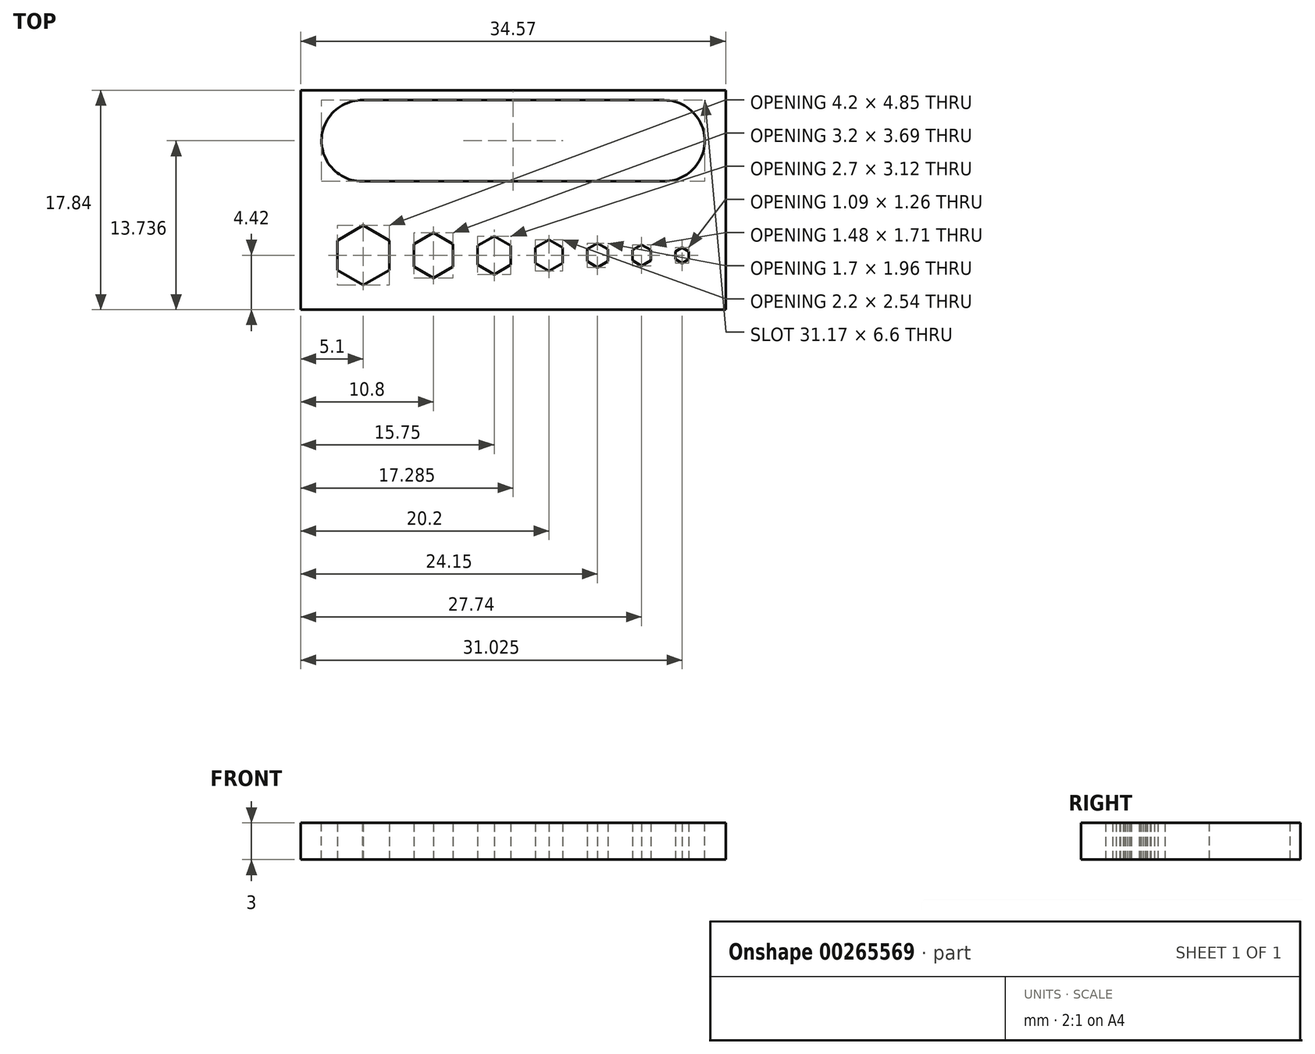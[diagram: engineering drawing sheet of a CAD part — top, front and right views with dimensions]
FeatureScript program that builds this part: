
annotation { "Feature Type Name" : "Feature", "Feature Type Description" : "" }
export const myFeature = defineFeature(function(context is Context, id is Id, definition is map)
    precondition{}
    {
        {
            var Q0;
            Q0=qCreatedBy(makeId("Top.planeOp"),FACE);
            var sketch = newSketch(context, id + "F0", { "sketchPlane" : qUnion([Q0])});
            skCircle(sketch, "E0.cCircle", {"center": v(0, 0) * mm, "radius": 1.1 * mm, "construction": true});
            skLineSegment(sketch, "E0.0", {"start": v(1.1, 0.64) * mm, "end": v(1.1, -0.64) * mm});
            skLineSegment(sketch, "E0.1", {"start": v(1.1, -0.64) * mm, "end": v(0, -1.27) * mm});
            skLineSegment(sketch, "E0.2", {"start": v(0, -1.27) * mm, "end": v(-1.1, -0.64) * mm});
            skLineSegment(sketch, "E0.3", {"start": v(-1.1, -0.64) * mm, "end": v(-1.1, 0.64) * mm});
            skLineSegment(sketch, "E0.4", {"start": v(-1.1, 0.64) * mm, "end": v(0, 1.27) * mm});
            skLineSegment(sketch, "E0.5", {"start": v(0, 1.27) * mm, "end": v(1.1, 0.64) * mm});
            skPoint(sketch, "E0.0.midPoint", {"position": v(1.1, 0) * mm});
            skCircle(sketch, "E1.cCircle", {"center": v(3.95, 0) * mm, "radius": 0.85 * mm, "construction": true});
            skLineSegment(sketch, "E1.0", {"start": v(4.8, 0.5) * mm, "end": v(4.8, -0.5) * mm});
            skLineSegment(sketch, "E1.1", {"start": v(4.8, -0.5) * mm, "end": v(3.95, -0.98) * mm});
            skLineSegment(sketch, "E1.2", {"start": v(3.95, -0.98) * mm, "end": v(3.1, -0.5) * mm});
            skLineSegment(sketch, "E1.3", {"start": v(3.1, -0.5) * mm, "end": v(3.1, 0.5) * mm});
            skLineSegment(sketch, "E1.4", {"start": v(3.1, 0.5) * mm, "end": v(3.95, 0.98) * mm});
            skLineSegment(sketch, "E1.5", {"start": v(3.95, 0.98) * mm, "end": v(4.8, 0.5) * mm});
            skPoint(sketch, "E1.0.midPoint", {"position": v(4.8, 0) * mm});
            skCircle(sketch, "E2.cCircle", {"center": v(7.54, 0) * mm, "radius": 0.74 * mm, "construction": true});
            skLineSegment(sketch, "E2.0", {"start": v(8.28, 0.43) * mm, "end": v(8.28, -0.43) * mm});
            skLineSegment(sketch, "E2.1", {"start": v(8.28, -0.43) * mm, "end": v(7.54, -0.85) * mm});
            skLineSegment(sketch, "E2.2", {"start": v(7.54, -0.85) * mm, "end": v(6.8, -0.43) * mm});
            skLineSegment(sketch, "E2.3", {"start": v(6.8, -0.43) * mm, "end": v(6.8, 0.43) * mm});
            skLineSegment(sketch, "E2.4", {"start": v(6.8, 0.43) * mm, "end": v(7.54, 0.85) * mm});
            skLineSegment(sketch, "E2.5", {"start": v(7.54, 0.85) * mm, "end": v(8.28, 0.43) * mm});
            skPoint(sketch, "E2.0.midPoint", {"position": v(8.28, 0) * mm});
            skCircle(sketch, "E3.cCircle", {"center": v(10.82, 0) * mm, "radius": 0.54 * mm, "construction": true});
            skLineSegment(sketch, "E3.0", {"start": v(11.37, 0.31) * mm, "end": v(11.37, -0.31) * mm});
            skLineSegment(sketch, "E3.1", {"start": v(11.37, -0.31) * mm, "end": v(10.82, -0.63) * mm});
            skLineSegment(sketch, "E3.2", {"start": v(10.82, -0.63) * mm, "end": v(10.28, -0.31) * mm});
            skLineSegment(sketch, "E3.3", {"start": v(10.28, -0.31) * mm, "end": v(10.28, 0.31) * mm});
            skLineSegment(sketch, "E3.4", {"start": v(10.28, 0.31) * mm, "end": v(10.83, 0.63) * mm});
            skLineSegment(sketch, "E3.5", {"start": v(10.83, 0.63) * mm, "end": v(11.37, 0.31) * mm});
            skPoint(sketch, "E3.0.midPoint", {"position": v(11.37, 0) * mm});
            skCircle(sketch, "E4.cCircle", {"center": v(-4.45, 0) * mm, "radius": 1.35 * mm, "construction": true});
            skLineSegment(sketch, "E4.0", {"start": v(-3.1, 0.78) * mm, "end": v(-3.1, -0.78) * mm});
            skLineSegment(sketch, "E4.1", {"start": v(-3.1, -0.78) * mm, "end": v(-4.45, -1.56) * mm});
            skLineSegment(sketch, "E4.2", {"start": v(-4.45, -1.56) * mm, "end": v(-5.8, -0.78) * mm});
            skLineSegment(sketch, "E4.3", {"start": v(-5.8, -0.78) * mm, "end": v(-5.8, 0.78) * mm});
            skLineSegment(sketch, "E4.4", {"start": v(-5.8, 0.78) * mm, "end": v(-4.45, 1.56) * mm});
            skLineSegment(sketch, "E4.5", {"start": v(-4.45, 1.56) * mm, "end": v(-3.1, 0.78) * mm});
            skPoint(sketch, "E4.0.midPoint", {"position": v(-3.1, 0) * mm});
            skCircle(sketch, "E5.cCircle", {"center": v(-9.4, 0) * mm, "radius": 1.6 * mm, "construction": true});
            skLineSegment(sketch, "E5.0", {"start": v(-7.8, 0.92) * mm, "end": v(-7.8, -0.92) * mm});
            skLineSegment(sketch, "E5.1", {"start": v(-7.8, -0.92) * mm, "end": v(-9.4, -1.85) * mm});
            skLineSegment(sketch, "E5.2", {"start": v(-9.4, -1.85) * mm, "end": v(-11, -0.92) * mm});
            skLineSegment(sketch, "E5.3", {"start": v(-11, -0.92) * mm, "end": v(-11, 0.92) * mm});
            skLineSegment(sketch, "E5.4", {"start": v(-11, 0.92) * mm, "end": v(-9.4, 1.85) * mm});
            skLineSegment(sketch, "E5.5", {"start": v(-9.4, 1.85) * mm, "end": v(-7.8, 0.92) * mm});
            skPoint(sketch, "E5.0.midPoint", {"position": v(-7.8, 0) * mm});
            skCircle(sketch, "E6.cCircle", {"center": v(-15.1, 0) * mm, "radius": 2.1 * mm, "construction": true});
            skPoint(sketch, "E6.cCircle.centerSnap0", {"position": v(-11, 0) * mm});
            skPoint(sketch, "E6.cCircle.perimeterSnap0", {"position": v(-11, 0) * mm});
            skLineSegment(sketch, "E6.0", {"start": v(-13, 1.21) * mm, "end": v(-13, -1.21) * mm});
            skLineSegment(sketch, "E6.1", {"start": v(-13, -1.21) * mm, "end": v(-15.1, -2.42) * mm});
            skLineSegment(sketch, "E6.2", {"start": v(-15.1, -2.42) * mm, "end": v(-17.2, -1.21) * mm});
            skLineSegment(sketch, "E6.3", {"start": v(-17.2, -1.21) * mm, "end": v(-17.2, 1.21) * mm});
            skLineSegment(sketch, "E6.4", {"start": v(-17.2, 1.21) * mm, "end": v(-15.1, 2.42) * mm});
            skLineSegment(sketch, "E6.5", {"start": v(-15.1, 2.42) * mm, "end": v(-13, 1.21) * mm});
            skPoint(sketch, "E6.0.midPoint", {"position": v(-13, 0) * mm});
            skPoint(sketch, "E6.0.midPoint.positionSnap0", {"position": v(-11, 0) * mm});
            skLineSegment(sketch, "E7.bottom", {"start": v(-20.2, 4.42) * mm, "end": v(14.37, 4.42) * mm});
            skLineSegment(sketch, "E7.top", {"start": v(-20.2, -4.42) * mm, "end": v(14.37, -4.42) * mm});
            skLineSegment(sketch, "E7.left", {"start": v(-20.2, 4.42) * mm, "end": v(-20.2, -4.42) * mm});
            skLineSegment(sketch, "E7.right", {"start": v(14.37, 4.42) * mm, "end": v(14.37, -4.42) * mm});
            skLineSegment(sketch, "E8.top", {"start": v(-20.2, 13.42) * mm, "end": v(14.37, 13.42) * mm});
            skLineSegment(sketch, "E8.left", {"start": v(-20.2, 4.42) * mm, "end": v(-20.2, 13.42) * mm});
            skLineSegment(sketch, "E8.right", {"start": v(14.37, 4.42) * mm, "end": v(14.37, 13.42) * mm});
            skPoint(sketch, "E9.startSnap0", {"position": v(-20.2, 8.92) * mm});
            skPoint(sketch, "E10", {"position": v(-15.2, 8.92) * mm});
            skPoint(sketch, "E11", {"position": v(9.37, 9.53) * mm});
            skSolve(sketch);
        }
        {
            var Q0;
            Q0 = qSketchRegion(id + "F0", true);
            extrude(context, id + "F1", {"entities" : qUnion([Q0]), "depth" : 3 * mm});
        }
        {
            var Q0;
            Q0=makeQuery(id+"F1.opExtrude","CAP_FACE",FACE,{"disambiguationData":[OSD([sQuery(id+"F0.wireOp",EDGE,"E0.0"),sQuery(id+"F0.wireOp",EDGE,"E0.1"),sQuery(id+"F0.wireOp",EDGE,"E0.2"),sQuery(id+"F0.wireOp",EDGE,"E0.3"),sQuery(id+"F0.wireOp",EDGE,"E0.4"),sQuery(id+"F0.wireOp",EDGE,"E0.5"),sQuery(id+"F0.wireOp",EDGE,"E1.0"),sQuery(id+"F0.wireOp",EDGE,"E1.1"),sQuery(id+"F0.wireOp",EDGE,"E1.2"),sQuery(id+"F0.wireOp",EDGE,"E1.3"),sQuery(id+"F0.wireOp",EDGE,"E1.4"),sQuery(id+"F0.wireOp",EDGE,"E1.5"),sQuery(id+"F0.wireOp",EDGE,"E2.0"),sQuery(id+"F0.wireOp",EDGE,"E2.1"),sQuery(id+"F0.wireOp",EDGE,"E2.2"),sQuery(id+"F0.wireOp",EDGE,"E2.3"),sQuery(id+"F0.wireOp",EDGE,"E2.4"),sQuery(id+"F0.wireOp",EDGE,"E2.5"),sQuery(id+"F0.wireOp",EDGE,"E3.0"),sQuery(id+"F0.wireOp",EDGE,"E3.1"),sQuery(id+"F0.wireOp",EDGE,"E3.2"),sQuery(id+"F0.wireOp",EDGE,"E3.3"),sQuery(id+"F0.wireOp",EDGE,"E3.4"),sQuery(id+"F0.wireOp",EDGE,"E3.5"),sQuery(id+"F0.wireOp",EDGE,"E4.0"),sQuery(id+"F0.wireOp",EDGE,"E4.1"),sQuery(id+"F0.wireOp",EDGE,"E4.2"),sQuery(id+"F0.wireOp",EDGE,"E4.3"),sQuery(id+"F0.wireOp",EDGE,"E4.4"),sQuery(id+"F0.wireOp",EDGE,"E4.5"),sQuery(id+"F0.wireOp",EDGE,"E5.0"),sQuery(id+"F0.wireOp",EDGE,"E5.1"),sQuery(id+"F0.wireOp",EDGE,"E5.2"),sQuery(id+"F0.wireOp",EDGE,"E5.3"),sQuery(id+"F0.wireOp",EDGE,"E5.4"),sQuery(id+"F0.wireOp",EDGE,"E5.5"),sQuery(id+"F0.wireOp",EDGE,"E6.0"),sQuery(id+"F0.wireOp",EDGE,"E6.1"),sQuery(id+"F0.wireOp",EDGE,"E6.2"),sQuery(id+"F0.wireOp",EDGE,"E6.3"),sQuery(id+"F0.wireOp",EDGE,"E6.4"),sQuery(id+"F0.wireOp",EDGE,"E6.5"),sQuery(id+"F0.wireOp",EDGE,"E7.top"),sQuery(id+"F0.wireOp",EDGE,"E7.left"),sQuery(id+"F0.wireOp",EDGE,"E7.right"),sQuery(id+"F0.wireOp",EDGE,"E8.top"),sQuery(id+"F0.wireOp",EDGE,"E8.left"),sQuery(id+"F0.wireOp",EDGE,"E8.right")])],"isStart":false});
            var sketch = newSketch(context, id + "F2", { "sketchPlane" : qUnion([Q0])});
            skPoint(sketch, "E12", {"position": v(-15.2, 9.32) * mm});
            skPoint(sketch, "E13", {"position": v(9.37, 9.32) * mm});
            skSolve(sketch);
        }
        {
            var Q0;
            Q0=sQuery(id+"F2.wireOp",VERTEX,"E12");
            var Q1;
            Q1=sQuery(id+"F2.wireOp",VERTEX,"E13");
            var Q2;
            Q2=makeQuery(id+"F1.opExtrude","SWEPT_BODY",BODY,{"disambiguationData":[OSD([sQuery(id+"F0.wireOp",EDGE,"E0.0"),sQuery(id+"F0.wireOp",EDGE,"E0.1"),sQuery(id+"F0.wireOp",EDGE,"E0.2"),sQuery(id+"F0.wireOp",EDGE,"E0.3"),sQuery(id+"F0.wireOp",EDGE,"E0.4"),sQuery(id+"F0.wireOp",EDGE,"E0.5"),sQuery(id+"F0.wireOp",EDGE,"E1.0"),sQuery(id+"F0.wireOp",EDGE,"E1.1"),sQuery(id+"F0.wireOp",EDGE,"E1.2"),sQuery(id+"F0.wireOp",EDGE,"E1.3"),sQuery(id+"F0.wireOp",EDGE,"E1.4"),sQuery(id+"F0.wireOp",EDGE,"E1.5"),sQuery(id+"F0.wireOp",EDGE,"E2.0"),sQuery(id+"F0.wireOp",EDGE,"E2.1"),sQuery(id+"F0.wireOp",EDGE,"E2.2"),sQuery(id+"F0.wireOp",EDGE,"E2.3"),sQuery(id+"F0.wireOp",EDGE,"E2.4"),sQuery(id+"F0.wireOp",EDGE,"E2.5"),sQuery(id+"F0.wireOp",EDGE,"E3.0"),sQuery(id+"F0.wireOp",EDGE,"E3.1"),sQuery(id+"F0.wireOp",EDGE,"E3.2"),sQuery(id+"F0.wireOp",EDGE,"E3.3"),sQuery(id+"F0.wireOp",EDGE,"E3.4"),sQuery(id+"F0.wireOp",EDGE,"E3.5"),sQuery(id+"F0.wireOp",EDGE,"E4.0"),sQuery(id+"F0.wireOp",EDGE,"E4.1"),sQuery(id+"F0.wireOp",EDGE,"E4.2"),sQuery(id+"F0.wireOp",EDGE,"E4.3"),sQuery(id+"F0.wireOp",EDGE,"E4.4"),sQuery(id+"F0.wireOp",EDGE,"E4.5"),sQuery(id+"F0.wireOp",EDGE,"E5.0"),sQuery(id+"F0.wireOp",EDGE,"E5.1"),sQuery(id+"F0.wireOp",EDGE,"E5.2"),sQuery(id+"F0.wireOp",EDGE,"E5.3"),sQuery(id+"F0.wireOp",EDGE,"E5.4"),sQuery(id+"F0.wireOp",EDGE,"E5.5"),sQuery(id+"F0.wireOp",EDGE,"E6.0"),sQuery(id+"F0.wireOp",EDGE,"E6.1"),sQuery(id+"F0.wireOp",EDGE,"E6.2"),sQuery(id+"F0.wireOp",EDGE,"E6.3"),sQuery(id+"F0.wireOp",EDGE,"E6.4"),sQuery(id+"F0.wireOp",EDGE,"E6.5"),sQuery(id+"F0.wireOp",EDGE,"E7.top"),sQuery(id+"F0.wireOp",EDGE,"E7.left"),sQuery(id+"F0.wireOp",EDGE,"E7.right"),sQuery(id+"F0.wireOp",EDGE,"E8.top"),sQuery(id+"F0.wireOp",EDGE,"E8.left"),sQuery(id+"F0.wireOp",EDGE,"E8.right")])]});
            hole(context, id + "F3", {"style" : HoleStyle.SIMPLE, "endStyle" : HoleEndStyle.THROUGH, "standardTappedOrClearance" : lookupTablePath({ "standard" : "ISO", "fit" : "Normal", "size" : "M6", "type" : "Clearance" }), "standardBlindInLast" : lookupTablePath({ "fit" : "Standard", "standard" : "ISO", "size" : "M6", "type" : "Clearance" }), "holeDiameter" : 6.6 * mm, "tappedDepth" : 12 * mm, "tapClearance" : 3, "locations" : qUnion([Q0, Q1]), "scope" : qUnion([Q2])});
        }
        {
            var Q0;
            Q0=makeQuery(id+"F1.opExtrude","CAP_FACE",FACE,{"disambiguationData":[OSD([sQuery(id+"F0.wireOp",EDGE,"E0.0"),sQuery(id+"F0.wireOp",EDGE,"E0.1"),sQuery(id+"F0.wireOp",EDGE,"E0.2"),sQuery(id+"F0.wireOp",EDGE,"E0.3"),sQuery(id+"F0.wireOp",EDGE,"E0.4"),sQuery(id+"F0.wireOp",EDGE,"E0.5"),sQuery(id+"F0.wireOp",EDGE,"E1.0"),sQuery(id+"F0.wireOp",EDGE,"E1.1"),sQuery(id+"F0.wireOp",EDGE,"E1.2"),sQuery(id+"F0.wireOp",EDGE,"E1.3"),sQuery(id+"F0.wireOp",EDGE,"E1.4"),sQuery(id+"F0.wireOp",EDGE,"E1.5"),sQuery(id+"F0.wireOp",EDGE,"E2.0"),sQuery(id+"F0.wireOp",EDGE,"E2.1"),sQuery(id+"F0.wireOp",EDGE,"E2.2"),sQuery(id+"F0.wireOp",EDGE,"E2.3"),sQuery(id+"F0.wireOp",EDGE,"E2.4"),sQuery(id+"F0.wireOp",EDGE,"E2.5"),sQuery(id+"F0.wireOp",EDGE,"E3.0"),sQuery(id+"F0.wireOp",EDGE,"E3.1"),sQuery(id+"F0.wireOp",EDGE,"E3.2"),sQuery(id+"F0.wireOp",EDGE,"E3.3"),sQuery(id+"F0.wireOp",EDGE,"E3.4"),sQuery(id+"F0.wireOp",EDGE,"E3.5"),sQuery(id+"F0.wireOp",EDGE,"E4.0"),sQuery(id+"F0.wireOp",EDGE,"E4.1"),sQuery(id+"F0.wireOp",EDGE,"E4.2"),sQuery(id+"F0.wireOp",EDGE,"E4.3"),sQuery(id+"F0.wireOp",EDGE,"E4.4"),sQuery(id+"F0.wireOp",EDGE,"E4.5"),sQuery(id+"F0.wireOp",EDGE,"E5.0"),sQuery(id+"F0.wireOp",EDGE,"E5.1"),sQuery(id+"F0.wireOp",EDGE,"E5.2"),sQuery(id+"F0.wireOp",EDGE,"E5.3"),sQuery(id+"F0.wireOp",EDGE,"E5.4"),sQuery(id+"F0.wireOp",EDGE,"E5.5"),sQuery(id+"F0.wireOp",EDGE,"E6.0"),sQuery(id+"F0.wireOp",EDGE,"E6.1"),sQuery(id+"F0.wireOp",EDGE,"E6.2"),sQuery(id+"F0.wireOp",EDGE,"E6.3"),sQuery(id+"F0.wireOp",EDGE,"E6.4"),sQuery(id+"F0.wireOp",EDGE,"E6.5"),sQuery(id+"F0.wireOp",EDGE,"E7.top"),sQuery(id+"F0.wireOp",EDGE,"E7.left"),sQuery(id+"F0.wireOp",EDGE,"E7.right"),sQuery(id+"F0.wireOp",EDGE,"E8.top"),sQuery(id+"F0.wireOp",EDGE,"E8.left"),sQuery(id+"F0.wireOp",EDGE,"E8.right")])],"isStart":false});
            var sketch = newSketch(context, id + "F4", { "sketchPlane" : qUnion([Q0])});
            skLineSegment(sketch, "E14", {"start": v(-15.13, 12.62) * mm, "end": v(9.37, 12.62) * mm});
            skLineSegment(sketch, "E15", {"start": v(9.37, 12.62) * mm, "end": v(9.37, 6.02) * mm});
            skLineSegment(sketch, "E16", {"start": v(9.37, 6.02) * mm, "end": v(-15.2, 6.02) * mm});
            skLineSegment(sketch, "E17", {"start": v(-15.2, 6.02) * mm, "end": v(-15.13, 12.62) * mm});
            skSolve(sketch);
        }
        {
            var Q0;
            {var subQ0=sQuery(id+"F4.wireOp",EDGE,"E14");Q0=makeQuery(id+"F4.imprint","IMPRINT",FACE,{"disambiguationData":[TD([[makeQuery(id+"F4.imprint","IMPRINT",EDGE,{"derivedFrom":subQ0}),-1.0]])]});}
            extrude(context, id + "F5", {"entities" : qUnion([Q0]), "operationType" : NewBodyOperationType.REMOVE, "oppositeDirection" : true, "depth" : 25 * mm});
        }
    });
